# Revit family: HVAC_Ductwork_Airzone_Motorized-Plenum_Mitsubishi-Heavy_Standard_4-Dampers
name_source: partatom
category: Mechanical Equipment
revit_build: Autodesk Revit 2016 (Build: 20150714_1515(x64)
units: mm (PartAtom-declared; Revit-internal decimal feet)

## family parameters
Always vertical = Yes
Cut with Voids When Loaded = No
OmniClass Number = 23.75.70.14
OmniClass Title = Air Ductwork
Part Type = Normal
Room Calculation Point = No
Round Connector Dimension = Use Diameter
Shared = No
Work Plane-Based = No

## types (2) — shared parameters
Apparent Load = 58 VA
Dampers Diameter = 200.000 mm
Dampers Length = 149.000 mm
Description = Airzone standard motorized plenum with neck that mechanically adapts to the main ducted AC units of Mitsubishi Heavy.
Disclaimer = All information provided in this model is reviewed before being published. However, Airzone cannot guarantee this model is error-free, therefore users are strongly encouraged to check for technical documentation and updates
Fresh Air Inlet Connection Height = 75.000 mm
Fresh Air Inlet Connection Offset Height = 48.305 mm
Fresh Air Inlet Connection Width = 175.000 mm
Insulated Body Height = 300.000 mm
Insulated Body Length = 1140.000 mm
Insulated Body Material = Metal -AIRZONE - Insulating Lining -Aluminum Finish
Insulated Body Width = 205.000 mm
Load Classification = Other
Main Control Board Depth = 57.000 mm
Main Control Board Height = 180.000 mm
Main Control Board Material = Plastic - AIRZONE - Smooth - Off-white
Main Control Board Width = 195.000 mm
Manufacturer = AIRZONE
Material = Metal - AIRZONE - Galvanized Sheet - Semi-polished
Neck Bottom Offset = 79.000 mm
Neck Height = 176.000 mm
Neck Length = 95.000 mm
Power Factor = 1
Product Comments = Refer to technical documentation for further details
Product Documentation Download URL = http://doc.airzone.es
Revit Model Version = 1.0
Type Image = <None>
Type Image Comments = Image available in product documentation download
URL = www.airzone.es
Voltage = 230 V

## per-type parameters (varying)
| type | Neck Side Offset | Neck Width |
| MHIST01M4 | 127.000 mm | 886.000 mm |
| MHIST01S4 | 227.000 mm | 686.000 mm |

note: column(s) folded — value = type name in every type: Model

## geometry (parser evidence)
native form markers: Extrusion x2, Sweep x3
no freeform markers — native parametric forms only
